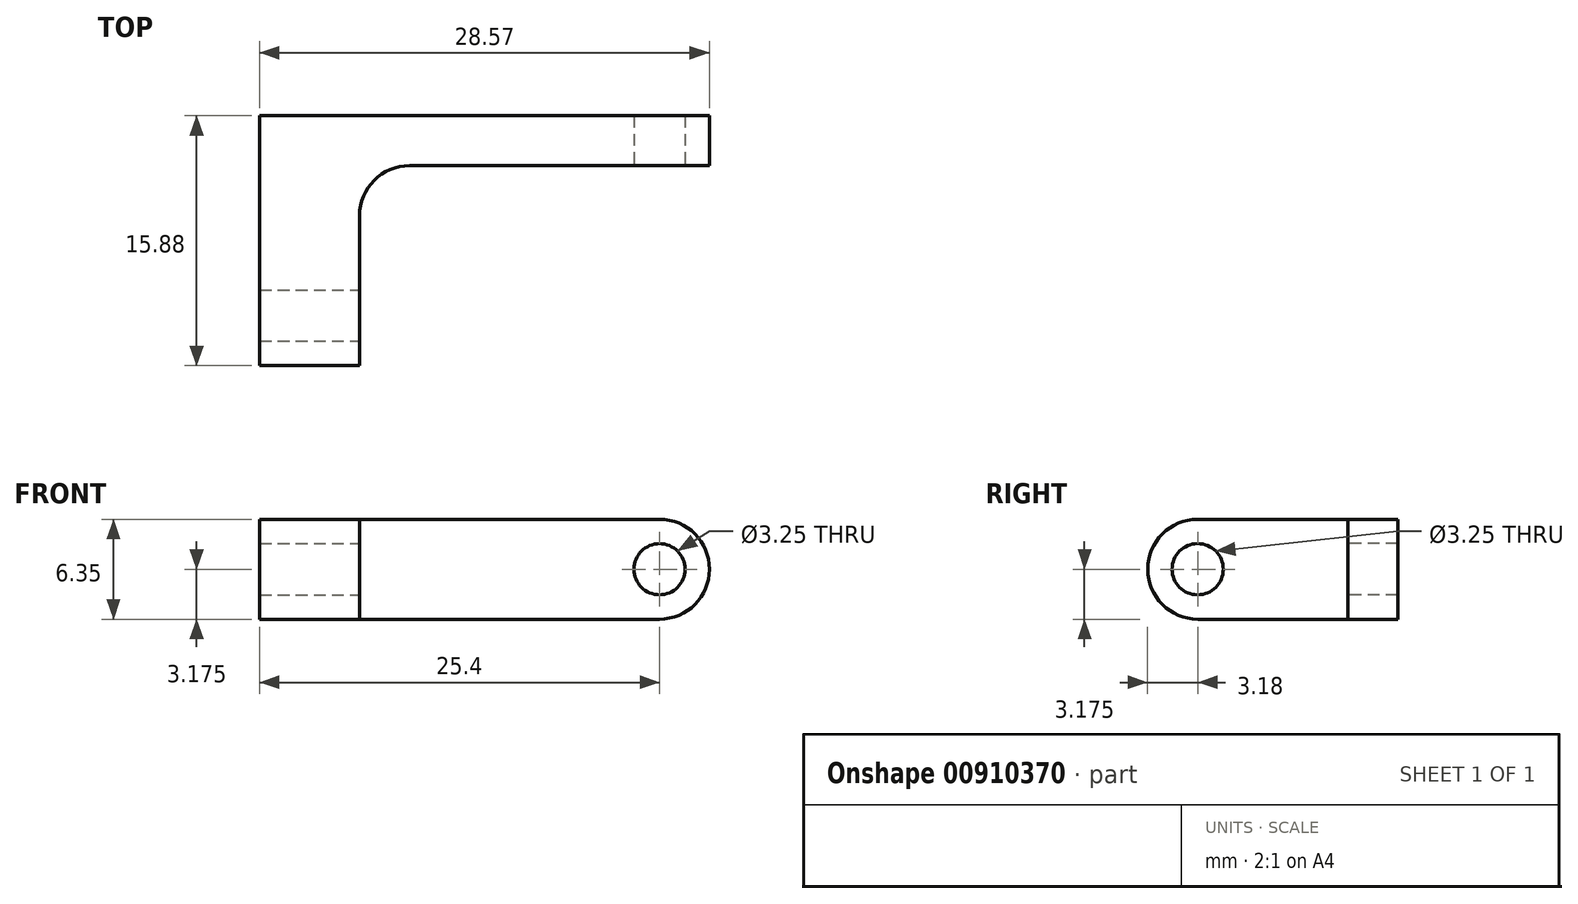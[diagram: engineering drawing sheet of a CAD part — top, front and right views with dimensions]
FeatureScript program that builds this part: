
annotation { "Feature Type Name" : "Feature", "Feature Type Description" : "" }
export const myFeature = defineFeature(function(context is Context, id is Id, definition is map)
    precondition{}
    {
        {
            var Q0;
            Q0=qCreatedBy(makeId("Top.planeOp"),FACE);
            var sketch = newSketch(context, id + "F0", { "sketchPlane" : qUnion([Q0])});
            skLineSegment(sketch, "E0", {"start": v(0, -15.87) * mm, "end": v(0, 0) * mm});
            skLineSegment(sketch, "E1", {"start": v(0, 0) * mm, "end": v(28.58, 0) * mm});
            skLineSegment(sketch, "E2", {"start": v(28.58, 0) * mm, "end": v(28.58, -3.17) * mm});
            skLineSegment(sketch, "E3", {"start": v(28.58, -3.17) * mm, "end": v(6.35, -3.18) * mm});
            skLineSegment(sketch, "E4", {"start": v(6.35, -3.18) * mm, "end": v(6.35, -15.87) * mm});
            skLineSegment(sketch, "E5", {"start": v(6.35, -15.87) * mm, "end": v(0, -15.87) * mm});
            skSolve(sketch);
        }
        {
            var Q0;
            Q0 = qSketchRegion(id + "F0", true);
            extrude(context, id + "F1", {"entities" : qUnion([Q0]), "depth" : 6.35 * mm, "offsetDistance" : 25.4 * mm});
        }
        {
            var Q0;
            Q0=makeQuery(id+"F1.opExtrude","CAP_EDGE",EDGE,{"disambiguationData":[OSD([sQuery(id+"F0.wireOp",EDGE,"E5")])],"isStart":false});
            var Q1;
            Q1=makeQuery(id+"F1.opExtrude","CAP_EDGE",EDGE,{"disambiguationData":[OSD([sQuery(id+"F0.wireOp",EDGE,"E5")])],"isStart":true});
            var Q2;
            Q2=makeQuery(id+"F1.opExtrude","CAP_EDGE",EDGE,{"disambiguationData":[OSD([sQuery(id+"F0.wireOp",EDGE,"E2")])],"isStart":false});
            var Q3;
            Q3=makeQuery(id+"F1.opExtrude","CAP_EDGE",EDGE,{"disambiguationData":[OSD([sQuery(id+"F0.wireOp",EDGE,"E2")])],"isStart":true});
            var Q4;
            Q4=makeQuery(id+"F1.opExtrude","SWEPT_EDGE",EDGE,{"disambiguationData":[OSD([sQuery(id+"F0.wireOp",EDGE,"E3"),sQuery(id+"F0.wireOp",EDGE,"E4")])]});
            fillet(context, id + "F2", {"entities" : qUnion([Q0, Q1, Q2, Q3, Q4]), "radius" : 3.17 * mm, "tangentPropagation" : true, "allowEdgeOverflow" : false});
        }
        {
            var Q0;
            Q0=makeQuery(id+"F1.opExtrude","SWEPT_FACE",FACE,{"disambiguationData":[OSD([sQuery(id+"F0.wireOp",EDGE,"E4")])]});
            var sketch = newSketch(context, id + "F3", { "sketchPlane" : qUnion([Q0])});
            skCircle(sketch, "E6", {"center": v(-12.7, 3.18) * mm, "radius": 1.63 * mm});
            skSolve(sketch);
        }
        {
            var Q0;
            Q0 = qSketchRegion(id + "F3", true);
            extrude(context, id + "F4", {"entities" : qUnion([Q0]), "operationType" : NewBodyOperationType.REMOVE, "endBound" : BoundingType.THROUGH_ALL, "oppositeDirection" : true, "depth" : 25.4 * mm, "offsetDistance" : 25.4 * mm});
        }
        {
            var Q0;
            Q0=makeQuery(id+"F1.opExtrude","SWEPT_FACE",FACE,{"disambiguationData":[OSD([sQuery(id+"F0.wireOp",EDGE,"E3")])]});
            var sketch = newSketch(context, id + "F5", { "sketchPlane" : qUnion([Q0])});
            skCircle(sketch, "E7", {"center": v(25.4, 3.18) * mm, "radius": 1.63 * mm});
            skSolve(sketch);
        }
        {
            var Q0;
            Q0 = qSketchRegion(id + "F5", true);
            extrude(context, id + "F6", {"entities" : qUnion([Q0]), "operationType" : NewBodyOperationType.REMOVE, "endBound" : BoundingType.THROUGH_ALL, "oppositeDirection" : true, "depth" : 25.4 * mm, "offsetDistance" : 25.4 * mm});
        }
    });
